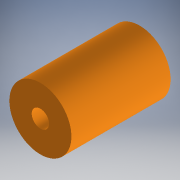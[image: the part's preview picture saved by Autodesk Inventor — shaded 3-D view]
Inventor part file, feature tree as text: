
AUTODESK INVENTOR PART (.ipt)
format: ipt  version: 2018 (Build 220112000, 112)  size: 110,592 bytes
history: native  units: mm
features: extrude x3, sketch x2
ambient origin geometry x8: Origin, YZ Plane, XZ Plane, XY Plane, X Axis, Y Axis, Z Axis, Center Point
bodies: Solid1 (feature_tree)
feature tree (5):
  sketch  "Sketch1"  dims[d0=2.8mm d1=10.0mm]
  extrude  "Extrusion1"  Depth=10.0mm
  extrude  "Extrusion2"  Depth=8.0mm TaperAngle=0.0deg
  extrude  "Extrusion3"  Depth=6.0mm
  sketch  "Sketch2"  dims[d2=16.0mm d3=0.0mm d4=8.0mm d5=0.0mm d6=6.0mm d7=6.38mm d8=4.45mm d9=0.18mm d10=6.0mm d11=0.0mm]
